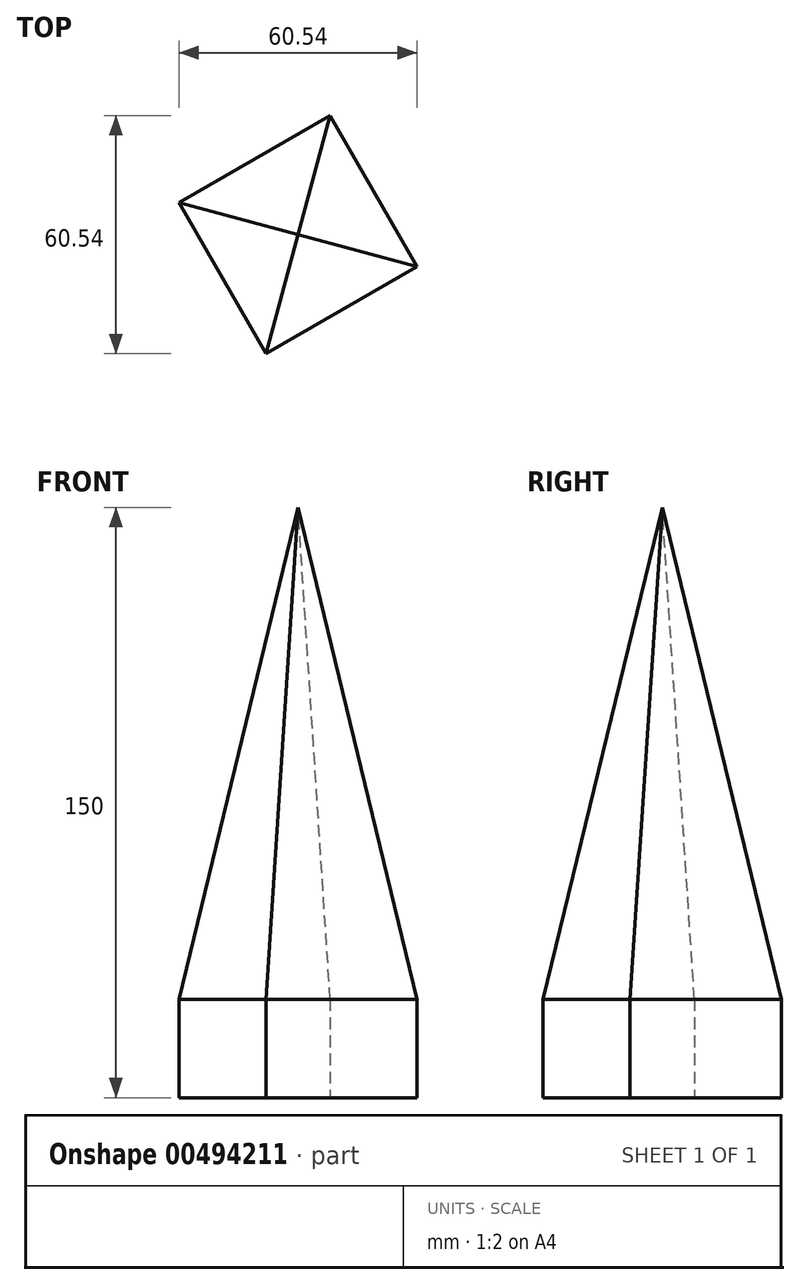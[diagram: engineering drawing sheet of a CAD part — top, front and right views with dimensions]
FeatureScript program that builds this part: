
annotation { "Feature Type Name" : "Feature", "Feature Type Description" : "" }
export const myFeature = defineFeature(function(context is Context, id is Id, definition is map)
    precondition{}
    {
        {
            var Q0;
            Q0=qCreatedBy(makeId("Top.planeOp"),FACE);
            var sketch = newSketch(context, id + "F0", { "sketchPlane" : qUnion([Q0])});
            skCircle(sketch, "E0.cCircle", {"center": v(0, 0) * mm, "radius": 22.17 * mm, "construction": true});
            skLineSegment(sketch, "E0.0", {"start": v(8.18, 30.27) * mm, "end": v(30.27, -8.18) * mm});
            skLineSegment(sketch, "E0.1", {"start": v(30.27, -8.18) * mm, "end": v(-8.18, -30.27) * mm});
            skLineSegment(sketch, "E0.2", {"start": v(-8.18, -30.27) * mm, "end": v(-30.27, 8.18) * mm});
            skLineSegment(sketch, "E0.3", {"start": v(-30.27, 8.18) * mm, "end": v(8.18, 30.27) * mm});
            skPoint(sketch, "E0.0.midPoint", {"position": v(19.22, 11.05) * mm});
            skSolve(sketch);
        }
        {
            var Q0;
            Q0=makeQuery(id+"F0.imprint","IMPRINT",FACE,{"disambiguationData":[TD([[makeQuery(id+"F0.imprint","IMPRINT",EDGE,{"derivedFrom":sQuery(id+"F0.wireOp",EDGE,"E0.0")}),-1.0]])]});
            extrude(context, id + "F1", {"entities" : qUnion([Q0]), "depth" : 25 * mm});
        }
        {
            var Q0;
            Q0=qCreatedBy(makeId("Top.planeOp"),FACE);
            cPlane(context, id + "F2", {"entities" : qUnion([Q0]), "cplaneType" : CPlaneType.OFFSET, "offset" : 150 * mm, "width" : 150 * mm, "height" : 150 * mm});
        }
        {
            var Q0;
            Q0=qCreatedBy(id+"F2.planeOp",FACE);
            var sketch = newSketch(context, id + "F3", { "sketchPlane" : qUnion([Q0])});
            skPoint(sketch, "E1", {"position": v(0, 0) * mm});
            skSolve(sketch);
        }
        {
            var Q1;
            Q1=makeQuery(id+"F1.opExtrude","CAP_FACE",FACE,{"disambiguationData":[OSD([sQuery(id+"F0.wireOp",EDGE,"E0.0"),sQuery(id+"F0.wireOp",EDGE,"E0.1"),sQuery(id+"F0.wireOp",EDGE,"E0.2"),sQuery(id+"F0.wireOp",EDGE,"E0.3")])],"isStart":false});
            var Q2;
            Q2=sQuery(id+"F3.wireOp",VERTEX,"E1");
            loft(context, id + "F4", {"operationType" : NewBodyOperationType.ADD, "sheetProfilesArray" : [{ "sheetProfileEntities" : qUnion([Q1]) }, { "sheetProfileEntities" : qUnion([Q2]) }]});
        }
    });
